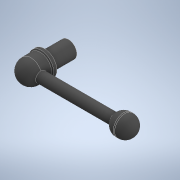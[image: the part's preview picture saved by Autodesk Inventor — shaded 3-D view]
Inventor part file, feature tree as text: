
AUTODESK INVENTOR PART (.ipt)
format: ipt  version: 2022 (Build 260153000, 153)  size: 151,040 bytes
history: native  units: mm
features: extrude x5, sketch x5, fillet x3, chamfer x1
ambient origin geometry x8: Origin, YZ Plane, XZ Plane, XY Plane, X Axis, Y Axis, Z Axis, Center Point
bodies: Solid1 (feature_tree)
feature tree (14):
  extrude  "Extrusion1"  Depth=6.5mm TaperAngle=0.0deg
  extrude  "Extrusion2"  Depth=2.0mm TaperAngle=0.0deg
  chamfer  "Chamfer1"  Distance=0.5mm Angle=45.0deg
  extrude  "Extrusion3"  Depth=5.5mm
  fillet  "Fillet1"  Radius=5.0mm
  extrude  "Extrusion4"  Depth=10.0mm
  extrude  "Extrusion5"  Depth=5.0mm
  fillet  "Fillet2"  Radius=5.0mm
  fillet  "Fillet3"  Radius=5.0mm
  sketch  "Sketch1"  dims[d0=8.0mm d1=6.5mm d2=0.0mm]
  sketch  "Sketch2"  dims[d3=12.0mm d4=2.0mm d5=0.0mm d6=0.5mm d7=2.0mm d8=45.0deg]
  sketch  "Sketch3"  dims[d9=10.0mm d10=0.0mm d11=5.5mm d12=5.0mm]
  sketch  "Sketch4"  dims[d13=40.0mm d14=0.0mm d15=10.0mm]
  sketch  "Sketch5"  dims[d16=10.0mm d17=0.0mm d18=5.0mm d19=5.0mm d20=5.0mm d21=0.0mm d22=0.5mm d23=0.872665mm]
